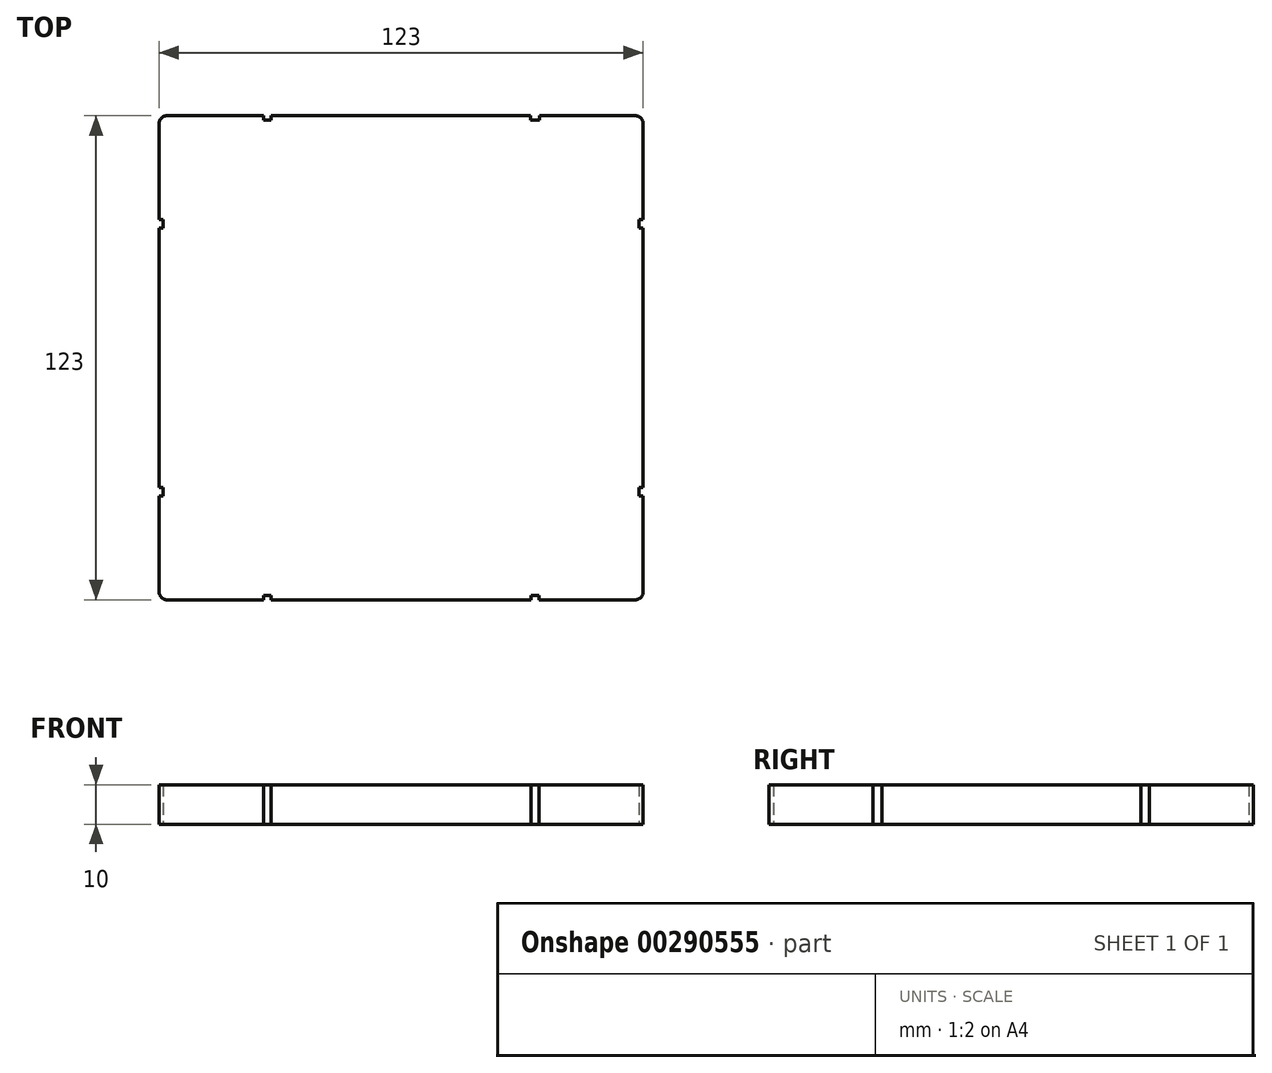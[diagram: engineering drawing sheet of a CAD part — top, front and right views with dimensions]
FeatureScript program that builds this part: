
annotation { "Feature Type Name" : "Feature", "Feature Type Description" : "" }
export const myFeature = defineFeature(function(context is Context, id is Id, definition is map)
    precondition{}
    {
        {
            var Q0;
            Q0=qCreatedBy(makeId("Top.planeOp"),FACE);
            var sketch = newSketch(context, id + "F0", { "sketchPlane" : qUnion([Q0])});
            skLineSegment(sketch, "E0.bottom", {"start": v(59.5, 61.5) * mm, "end": v(-59.5, 61.5) * mm});
            skLineSegment(sketch, "E0.top", {"start": v(59.5, -61.5) * mm, "end": v(-59.5, -61.5) * mm});
            skLineSegment(sketch, "E0.left", {"start": v(61.5, 59.5) * mm, "end": v(61.5, -59.5) * mm});
            skLineSegment(sketch, "E0.right", {"start": v(-61.5, 59.5) * mm, "end": v(-61.5, -59.5) * mm});
            skPoint(sketch, "E1.visualSharp", {"position": v(-61.5, 61.5) * mm});
            skArc(sketch, "E1.filletArc", {"start": v(-59.5, 61.5) * mm, "mid": v(-60.91, 60.91) * mm, "end": v(-61.5, 59.5) * mm});
            skPoint(sketch, "E2.visualSharp", {"position": v(61.5, 61.5) * mm});
            skArc(sketch, "E2.filletArc", {"start": v(61.5, 59.5) * mm, "mid": v(60.91, 60.91) * mm, "end": v(59.5, 61.5) * mm});
            skPoint(sketch, "E3.visualSharp", {"position": v(61.5, -61.5) * mm});
            skArc(sketch, "E3.filletArc", {"start": v(59.5, -61.5) * mm, "mid": v(60.91, -60.91) * mm, "end": v(61.5, -59.5) * mm});
            skPoint(sketch, "E4.visualSharp", {"position": v(-61.5, -61.5) * mm});
            skArc(sketch, "E4.filletArc", {"start": v(-61.5, -59.5) * mm, "mid": v(-60.91, -60.91) * mm, "end": v(-59.5, -61.5) * mm});
            skSolve(sketch);
        }
        {
            var Q0;
            Q0=qCreatedBy(makeId("Top.planeOp"),FACE);
            var sketch = newSketch(context, id + "F1", { "sketchPlane" : qUnion([Q0])});
            skLineSegment(sketch, "E5", {"start": v(-34, 79.9) * mm, "end": v(-34, -79.91) * mm, "construction": true});
            skLineSegment(sketch, "E6", {"start": v(34, -79.91) * mm, "end": v(34, 79.84) * mm, "construction": true});
            skLineSegment(sketch, "E7", {"start": v(-79.51, 34) * mm, "end": v(79.76, 34) * mm, "construction": true});
            skLineSegment(sketch, "E8", {"start": v(-79.78, -34) * mm, "end": v(79.98, -34) * mm, "construction": true});
            skLineSegment(sketch, "E9.bottom", {"start": v(-33, 62.6) * mm, "end": v(-35, 62.6) * mm});
            skLineSegment(sketch, "E9.top", {"start": v(-33, 60.4) * mm, "end": v(-35, 60.4) * mm});
            skLineSegment(sketch, "E9.left", {"start": v(-33, 62.6) * mm, "end": v(-33, 60.4) * mm});
            skLineSegment(sketch, "E9.right", {"start": v(-35, 62.6) * mm, "end": v(-35, 60.4) * mm});
            skPoint(sketch, "E9.middle", {"position": v(-34, 61.5) * mm});
            skLineSegment(sketch, "E10.bottom", {"start": v(35.1, 62.6) * mm, "end": v(32.9, 62.6) * mm});
            skLineSegment(sketch, "E10.top", {"start": v(35.1, 60.4) * mm, "end": v(32.9, 60.4) * mm});
            skLineSegment(sketch, "E10.left", {"start": v(35.1, 62.6) * mm, "end": v(35.1, 60.4) * mm});
            skLineSegment(sketch, "E10.right", {"start": v(32.9, 62.6) * mm, "end": v(32.9, 60.4) * mm});
            skPoint(sketch, "E10.middle", {"position": v(34, 61.5) * mm});
            skLineSegment(sketch, "E11.bottom", {"start": v(62.6, 32.9) * mm, "end": v(60.4, 32.9) * mm});
            skLineSegment(sketch, "E11.top", {"start": v(62.6, 35.1) * mm, "end": v(60.4, 35.1) * mm});
            skLineSegment(sketch, "E11.left", {"start": v(62.6, 32.9) * mm, "end": v(62.6, 35.1) * mm});
            skLineSegment(sketch, "E11.right", {"start": v(60.4, 32.9) * mm, "end": v(60.4, 35.1) * mm});
            skPoint(sketch, "E11.middle", {"position": v(61.5, 34) * mm});
            skLineSegment(sketch, "E12.bottom", {"start": v(62.6, -35.1) * mm, "end": v(60.4, -35.1) * mm});
            skLineSegment(sketch, "E12.top", {"start": v(62.6, -32.9) * mm, "end": v(60.4, -32.9) * mm});
            skLineSegment(sketch, "E12.left", {"start": v(62.6, -35.1) * mm, "end": v(62.6, -32.9) * mm});
            skLineSegment(sketch, "E12.right", {"start": v(60.4, -35.1) * mm, "end": v(60.4, -32.9) * mm});
            skPoint(sketch, "E12.middle", {"position": v(61.5, -34) * mm});
            skLineSegment(sketch, "E13.bottom", {"start": v(35, -62.6) * mm, "end": v(33, -62.6) * mm});
            skLineSegment(sketch, "E13.top", {"start": v(35, -60.4) * mm, "end": v(33, -60.4) * mm});
            skLineSegment(sketch, "E13.left", {"start": v(35, -62.6) * mm, "end": v(35, -60.4) * mm});
            skLineSegment(sketch, "E13.right", {"start": v(33, -62.6) * mm, "end": v(33, -60.4) * mm});
            skPoint(sketch, "E13.middle", {"position": v(34, -61.5) * mm});
            skLineSegment(sketch, "E14.bottom", {"start": v(-33, -62.6) * mm, "end": v(-35, -62.6) * mm});
            skLineSegment(sketch, "E14.top", {"start": v(-33, -60.4) * mm, "end": v(-35, -60.4) * mm});
            skLineSegment(sketch, "E14.left", {"start": v(-33, -62.6) * mm, "end": v(-33, -60.4) * mm});
            skLineSegment(sketch, "E14.right", {"start": v(-35, -62.6) * mm, "end": v(-35, -60.4) * mm});
            skPoint(sketch, "E14.middle", {"position": v(-34, -61.5) * mm});
            skLineSegment(sketch, "E15.bottom", {"start": v(-60.5, -32.9) * mm, "end": v(-62.5, -32.9) * mm});
            skLineSegment(sketch, "E15.top", {"start": v(-60.5, -35.1) * mm, "end": v(-62.5, -35.1) * mm});
            skLineSegment(sketch, "E15.left", {"start": v(-60.5, -32.9) * mm, "end": v(-60.5, -35.1) * mm});
            skLineSegment(sketch, "E15.right", {"start": v(-62.5, -32.9) * mm, "end": v(-62.5, -35.1) * mm});
            skPoint(sketch, "E15.middle", {"position": v(-61.5, -34) * mm});
            skLineSegment(sketch, "E16.bottom", {"start": v(-60.5, 35.1) * mm, "end": v(-62.5, 35.1) * mm});
            skLineSegment(sketch, "E16.top", {"start": v(-60.5, 32.9) * mm, "end": v(-62.5, 32.9) * mm});
            skLineSegment(sketch, "E16.left", {"start": v(-60.5, 35.1) * mm, "end": v(-60.5, 32.9) * mm});
            skLineSegment(sketch, "E16.right", {"start": v(-62.5, 35.1) * mm, "end": v(-62.5, 32.9) * mm});
            skPoint(sketch, "E16.middle", {"position": v(-61.5, 34) * mm});
            skSolve(sketch);
        }
        {
            var Q0;
            Q0=makeQuery(id+"F0.imprint","IMPRINT",FACE,{"disambiguationData":[TD([[makeQuery(id+"F0.imprint","IMPRINT",EDGE,{"derivedFrom":sQuery(id+"F0.wireOp",EDGE,"E0.bottom")}),1.0]])]});
            extrude(context, id + "F2", {"entities" : qUnion([Q0]), "depth" : 10 * mm});
        }
        {
            var Q0;
            Q0=qSketchRegion(id+"F1",true);
            extrude(context, id + "F3", {"entities" : qUnion([Q0]), "operationType" : NewBodyOperationType.REMOVE, "depth" : 10 * mm});
        }
    });
